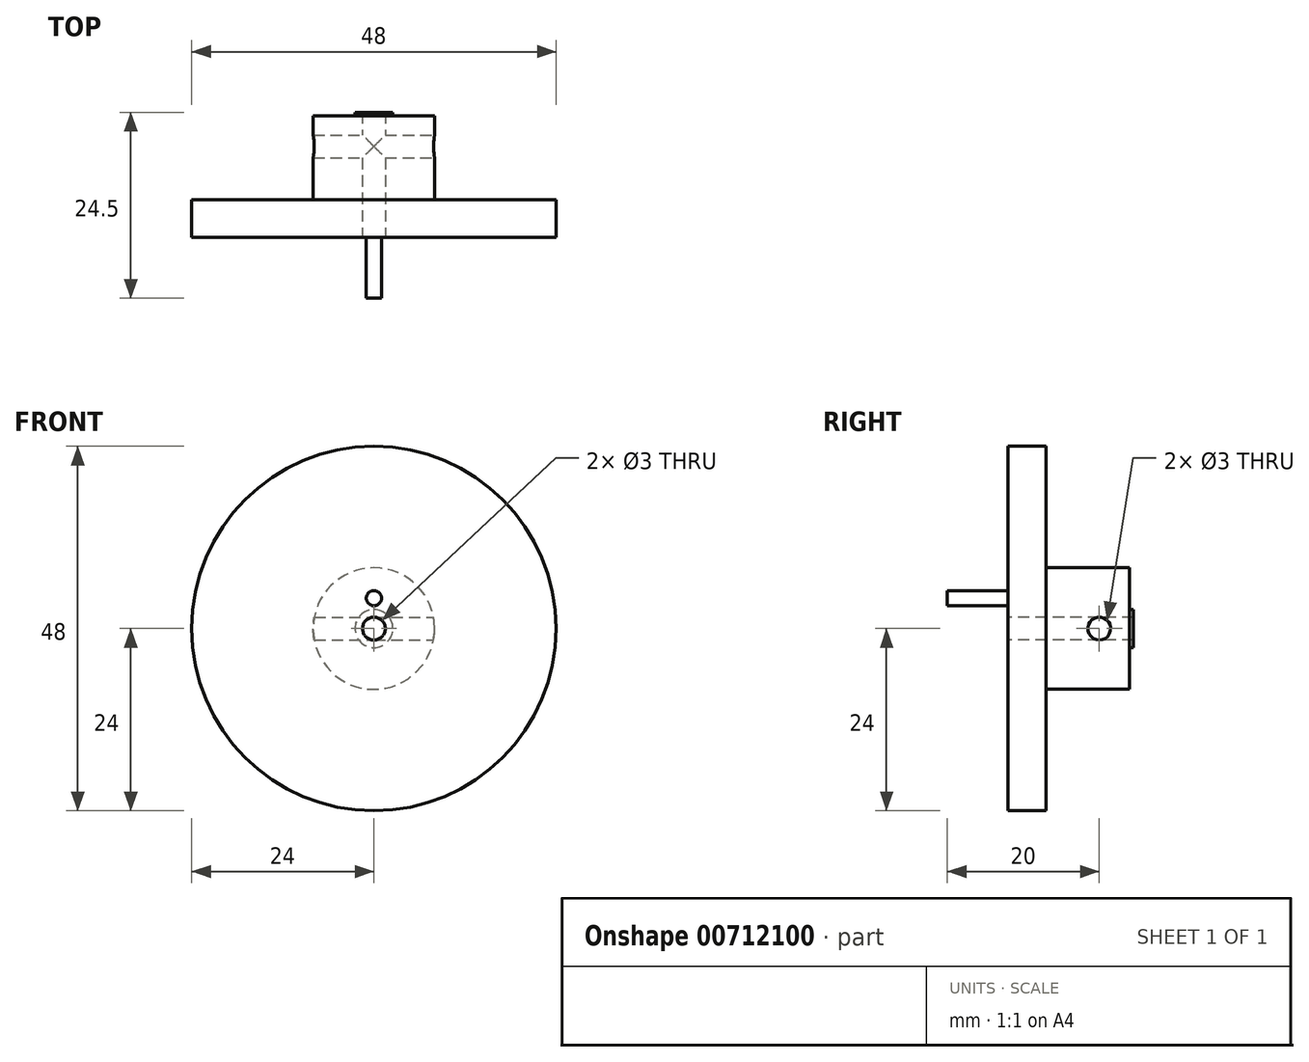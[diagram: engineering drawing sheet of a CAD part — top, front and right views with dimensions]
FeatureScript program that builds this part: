
annotation { "Feature Type Name" : "Feature", "Feature Type Description" : "" }
export const myFeature = defineFeature(function(context is Context, id is Id, definition is map)
    precondition{}
    {
        {
            var Q0;
            Q0=qCreatedBy(makeId("Front.planeOp"),FACE);
            var sketch = newSketch(context, id + "F0", { "sketchPlane" : qUnion([Q0])});
            skCircle(sketch, "E0", {"center": v(0, 0) * mm, "radius": 24 * mm});
            skCircle(sketch, "E1", {"center": v(0, 0) * mm, "radius": 8 * mm});
            skSolve(sketch);
        }
        {
            var Q0;
            Q0=makeQuery(id+"F0.imprint","IMPRINT",FACE,{"disambiguationData":[TD([[makeQuery(id+"F0.imprint","IMPRINT",EDGE,{"derivedFrom":sQuery(id+"F0.wireOp",EDGE,"E0")}),1.0]])]});
            var Q1;
            Q1=makeQuery(id+"F0.imprint","IMPRINT",FACE,{"disambiguationData":[TD([[makeQuery(id+"F0.imprint","IMPRINT",EDGE,{"derivedFrom":sQuery(id+"F0.wireOp",EDGE,"E1")}),1.0]])]});
            extrude(context, id + "F1", {"entities" : qUnion([Q0, Q1]), "depth" : 5 * mm, "offsetDistance" : 25 * mm});
        }
        {
            var Q0;
            Q0=makeQuery(id+"F0.imprint","IMPRINT",FACE,{"disambiguationData":[TD([[makeQuery(id+"F0.imprint","IMPRINT",EDGE,{"derivedFrom":sQuery(id+"F0.wireOp",EDGE,"E1")}),1.0]])]});
            extrude(context, id + "F2", {"entities" : qUnion([Q0]), "operationType" : NewBodyOperationType.ADD, "oppositeDirection" : true, "depth" : 11 * mm, "offsetDistance" : 25 * mm});
        }
        {
            var Q0;
            Q0=makeQuery(id+"F2.opExtrude","CAP_FACE",FACE,{"disambiguationData":[OSD([sQuery(id+"F0.wireOp",EDGE,"E1")])],"isStart":false});
            var sketch = newSketch(context, id + "F3", { "sketchPlane" : qUnion([Q0])});
            skCircle(sketch, "E2", {"center": v(0, 0) * mm, "radius": 2.5 * mm});
            skSolve(sketch);
        }
        {
            var Q0;
            Q0=makeQuery(id+"F3.imprint","IMPRINT",FACE,{"disambiguationData":[TD([[makeQuery(id+"F3.imprint","IMPRINT",EDGE,{"derivedFrom":sQuery(id+"F3.wireOp",EDGE,"E2")}),1.0]])]});
            extrude(context, id + "F4", {"entities" : qUnion([Q0]), "operationType" : NewBodyOperationType.ADD, "depth" : .5 * mm, "offsetDistance" : 25 * mm});
        }
        {
            var Q0;
            Q0=makeQuery(id+"F1.opExtrude","CAP_FACE",FACE,{"disambiguationData":[OSD([sQuery(id+"F0.wireOp",EDGE,"E0")])],"isStart":false});
            var sketch = newSketch(context, id + "F5", { "sketchPlane" : qUnion([Q0])});
            skCircle(sketch, "E3", {"center": v(0, 0) * mm, "radius": 1.5 * mm});
            skLineSegment(sketch, "E4", {"start": v(12.53, 0) * mm, "end": v(-19.66, 0) * mm, "construction": true});
            skLineSegment(sketch, "E5.0", {"start": v(12.53, 4) * mm, "end": v(-19.66, 4) * mm, "construction": true});
            skCircle(sketch, "E6", {"center": v(0, 4) * mm, "radius": 1 * mm});
            skSolve(sketch);
        }
        {
            var Q0;
            Q0=makeQuery(id+"F5.imprint","IMPRINT",FACE,{"disambiguationData":[TD([[makeQuery(id+"F5.imprint","IMPRINT",EDGE,{"derivedFrom":sQuery(id+"F5.wireOp",EDGE,"E3")}),1.0]])]});
            extrude(context, id + "F6", {"entities" : qUnion([Q0]), "operationType" : NewBodyOperationType.REMOVE, "oppositeDirection" : true, "depth" : 25 * mm, "offsetDistance" : 25 * mm});
        }
        {
            var Q0;
            Q0=makeQuery(id+"F5.imprint","IMPRINT",FACE,{"disambiguationData":[TD([[makeQuery(id+"F5.imprint","IMPRINT",EDGE,{"derivedFrom":sQuery(id+"F5.wireOp",EDGE,"E6")}),1.0]])]});
            extrude(context, id + "F7", {"entities" : qUnion([Q0]), "operationType" : NewBodyOperationType.ADD, "depth" : 8 * mm, "offsetDistance" : 25 * mm});
        }
        {
            var Q0;
            Q0=qCreatedBy(makeId("Right.planeOp"),FACE);
            var sketch = newSketch(context, id + "F8", { "sketchPlane" : qUnion([Q0])});
            skCircle(sketch, "E7", {"center": v(7, 0) * mm, "radius": 1.5 * mm});
            skSolve(sketch);
        }
        {
            var Q0;
            Q0 = qSketchRegion(id + "F8", true);
            extrude(context, id + "F9", {"entities" : qUnion([Q0]), "operationType" : NewBodyOperationType.REMOVE, "endBound" : BoundingType.THROUGH_ALL, "oppositeDirection" : true, "depth" : 25 * mm, "offsetDistance" : 25 * mm, "hasSecondDirection" : true, "secondDirectionBound" : BoundingType.THROUGH_ALL, "secondDirectionOppositeDirection" : false, "secondDirectionDepth" : 25 * mm});
        }
    });
